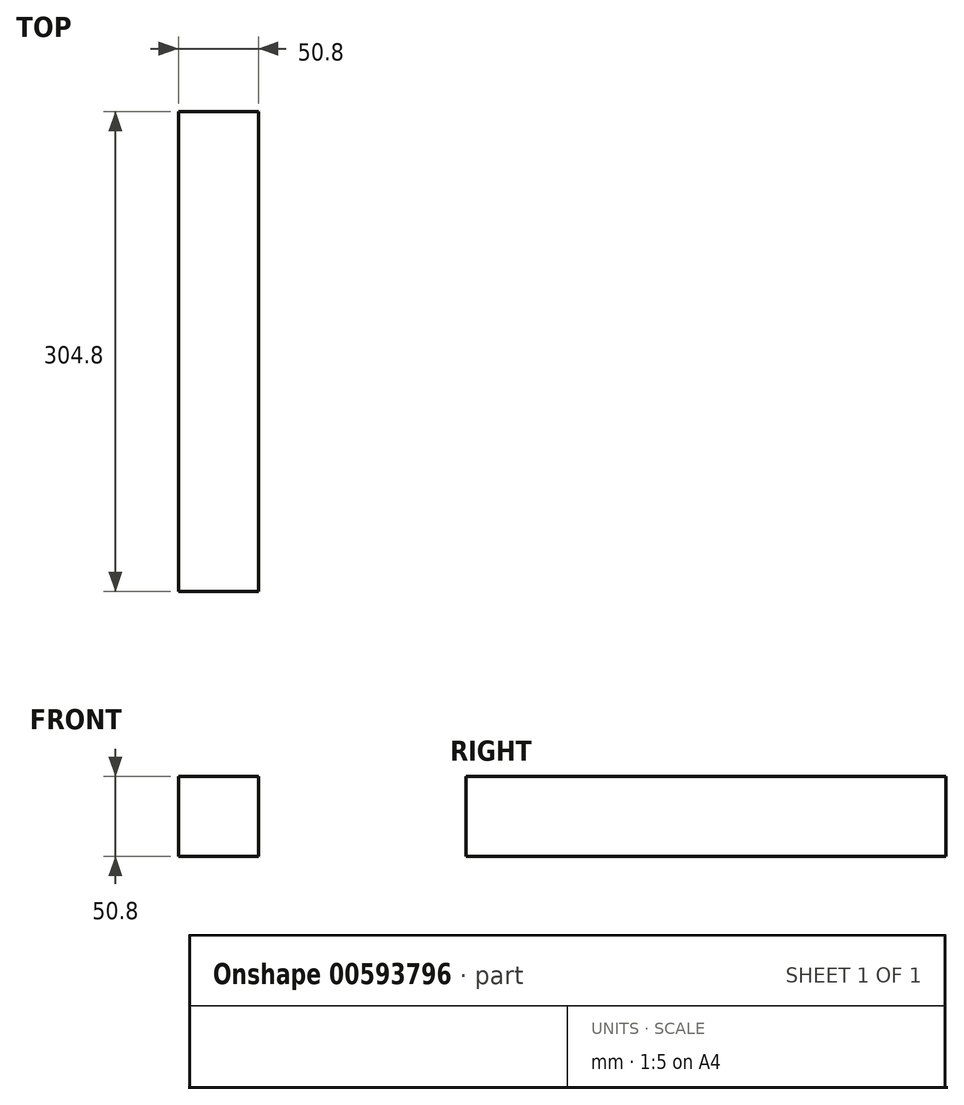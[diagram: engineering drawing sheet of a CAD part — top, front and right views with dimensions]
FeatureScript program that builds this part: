
annotation { "Feature Type Name" : "Feature", "Feature Type Description" : "" }
export const myFeature = defineFeature(function(context is Context, id is Id, definition is map)
    precondition{}
    {
        {
            var Q0;
            Q0=qCreatedBy(makeId("Top.planeOp"),FACE);
            var sketch = newSketch(context, id + "F0", { "sketchPlane" : qUnion([Q0])});
            skLineSegment(sketch, "E0.bottom", {"start": v(-57.9, 211.54) * mm, "end": v(-7.1, 211.54) * mm});
            skLineSegment(sketch, "E0.top", {"start": v(-57.9, -93.26) * mm, "end": v(-7.1, -93.26) * mm});
            skLineSegment(sketch, "E0.left", {"start": v(-57.9, 211.54) * mm, "end": v(-57.9, -93.26) * mm});
            skLineSegment(sketch, "E0.right", {"start": v(-7.1, 211.54) * mm, "end": v(-7.1, -93.26) * mm});
            skSolve(sketch);
        }
        {
            var Q0;
            Q0 = qSketchRegion(id + "F0", true);
            extrude(context, id + "F1", {"entities" : qUnion([Q0]), "depth" : 50.8 * mm, "offsetDistance" : 25.4 * mm});
        }
    });
